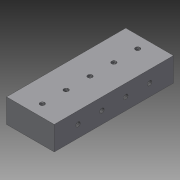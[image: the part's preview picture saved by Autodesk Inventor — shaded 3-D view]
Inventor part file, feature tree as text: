
AUTODESK INVENTOR PART (.ipt)
format: ipt  version: 2015 (Build 190159000, 159)  size: 101,888 bytes
history: native  units: in
note: dims shown in document units (in); Inventor stores cm internally (conversion verified against a paired STEP export)
features: sketch x3, hole x2, extrude x1
ambient origin geometry x8: Origin, YZ Plane, XZ Plane, XY Plane, X Axis, Y Axis, Z Axis, Center Point
bodies: Solid1 (feature_tree)
feature tree (6):
  extrude  "Extrusion1"  Depth=1.0in
  hole  "Hole1"  [1 undecoded]
  hole  "Hole2"  [1 undecoded]
  sketch  "Sketch1"  dims[d0=2.5in d1=1.0in]
  sketch  "Sketch2"  dims[d2=0.5in d3=0.0in d4=0.5in]
  sketch  "Sketch3"  dims[d5=0.5in d6=0.5in d8=0.097in d9=1.0in d10=0.375in d11=0.25in d12=0.5635in d13=0.346in d14=0.8108in d15=0.25in d16=0.5in d17=0.5in d18=0.5in d19=0.5in d20=0.097in d21=0.5in d22=0.375in d23=0.25in d24=0.5635in d25=0.346in d26=0.8108in]
note: 2 required parameter values undecoded (feature->parameter linkage not recoverable at this tier; creation-order binding heuristic only, values carry confidence <= 0.55)
